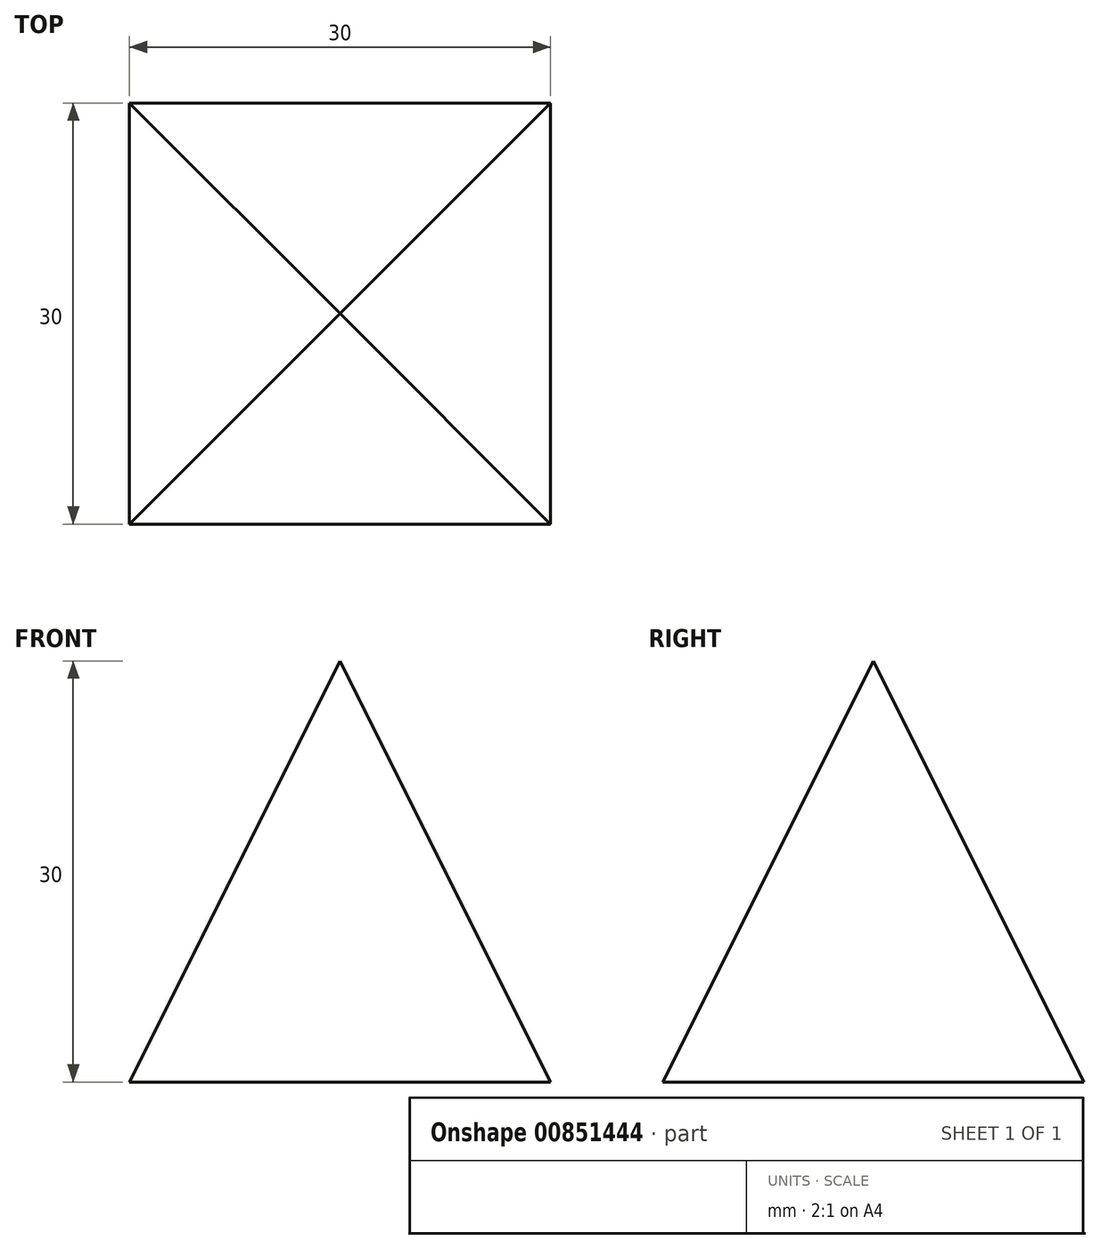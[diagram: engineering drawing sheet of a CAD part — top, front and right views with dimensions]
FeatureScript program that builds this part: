
annotation { "Feature Type Name" : "Feature", "Feature Type Description" : "" }
export const myFeature = defineFeature(function(context is Context, id is Id, definition is map)
    precondition{}
    {
        {
            var Q0;
            Q0=qCreatedBy(makeId("Top.planeOp"),FACE);
            var sketch = newSketch(context, id + "F0", { "sketchPlane" : qUnion([Q0])});
            skLineSegment(sketch, "E0.bottom", {"start": v(15, 15) * mm, "end": v(-15, 15) * mm});
            skLineSegment(sketch, "E0.top", {"start": v(15, -15) * mm, "end": v(-15, -15) * mm});
            skLineSegment(sketch, "E0.left", {"start": v(15, 15) * mm, "end": v(15, -15) * mm});
            skLineSegment(sketch, "E0.right", {"start": v(-15, 15) * mm, "end": v(-15, -15) * mm});
            skPoint(sketch, "E0.middle", {"position": v(0, 0) * mm});
            skSolve(sketch);
        }
        {
            var Q0;
            Q0=qCreatedBy(makeId("Top.planeOp"),FACE);
            cPlane(context, id + "F1", {"entities" : qUnion([Q0]), "cplaneType" : CPlaneType.OFFSET, "offset" : 30 * mm, "width" : 150 * mm, "height" : 150 * mm});
        }
        {
            var Q0;
            Q0=qCreatedBy(id+"F1.planeOp",FACE);
            var sketch = newSketch(context, id + "F2", { "sketchPlane" : qUnion([Q0])});
            skPoint(sketch, "E1", {"position": v(0, 0) * mm});
            skSolve(sketch);
        }
        {
            var Q0;
            Q0=makeQuery(id+"F0.imprint","IMPRINT",FACE,{"disambiguationData":[TD([[makeQuery(id+"F0.imprint","IMPRINT",EDGE,{"derivedFrom":sQuery(id+"F0.wireOp",EDGE,"E0.bottom")}),1.0]])]});
            var Q1;
            Q1=sQuery(id+"F2.wireOp",VERTEX,"E1");
            loft(context, id + "F3", {"sheetProfilesArray" : [{ "sheetProfileEntities" : qUnion([Q0]) }, { "sheetProfileEntities" : qUnion([Q1]) }]});
        }
    });
